# Revit family: BE_84401_de_DE
name_source: partatom
category: Leuchten
revit_build: Autodesk Revit 2015 (Build: 20160512_0715(x64)
units: mm (PartAtom-declared; Revit-internal decimal feet)

## types (4) — shared parameters
AC/DC = AC/DC
Aktualisierung = 2017-07-06T04:09:10
Anschlussleitung = 6.0 m X05BQ-F 4 × 1²
BEGA_Dummy = Nein
BEGA_IES = Ja
BEGA_IES1 = Ja
BEGA_IES2 = Ja
BEGA_IES3 = Ja
BEGA_Intern = Ja
BEGA_Intern_Konstruktion = Ja
BEGA_Intern_an = Ja
BEGA_Intern_aus = Ja
Beschreibung = Aufsatzleuchte
Beschreibung_Sonderanfertigung = Hier können Sie Informationen zur Sonderanfertigung eintragen.
CE_Konformität = ja
Einstecktiefe = 60 mm
Energieeffizienzklasse = LED A++ - A
Farbfilter = 16777215
Farbtemperaturverschiebung bei Dämpfen der Lampe = <Keine Auswahl>
Farbwiedergabeindex = Ra > 80
Frequenz = 0/50-60 Hz
Gewicht = 14.6 kg
Hersteller = BEGA
Lampe = LED 23.4 W
Lastklassifizierung = Beleuchtung
Lebensdauerkriterien = L70B50 @ 25 °C = 310000 h
Logo = BEGA_Logo.png
M_W = Nein
Material_02 = BEGA_Oberfläche_Silber_matt
Material_03 = BEGA_Oberfläche_Weiss_matt
Material_06 = BEGA_Oberfläche_Edelstahl_gebürstet
Material_09 = BEGA_Glas_klar
Material_10 = BEGA_Glas_matt
Material_11 = BEGA_Glas_opal
Material_15 = BEGA_Leuchtmedium_matt
Material_17 = BEGA_Reflektor
Material_18 = BEGA_Gummi_schwarz
Neigungswinkel = 0.00°
Produktdatenblatt = http://www.bega.de
Scheinlast = 0 VA
Schutzart = IP 65
Schutzklasse = II
Sonderanfertigung = Nein
Spannung = 240 V
Typenbild = 84401.png
URL = http://www.bega.de
Umgebungstemperatur = 25 °C
Windangriffsfläche = 0.14 m²
zero-valued in all types: BEGA_IES_X1, BEGA_IES_X2, BEGA_IES_Y1, BEGA_IES_Y2, BEGA_IES_Z1, BEGA_IES_Z2, Vorgabe-Ansicht

## per-type parameters (varying)
| type | Bestellnummer | Datei für fotometrisches Netz | Farbtemperatur | LED_Modulbezeichnung | Lampenlichtstrom | Leuchtenlichtstrom | M_A | M_G | Modell |
| BEGA_84401_Grafit_K3 | 84401K3 | BE_84401K3.IES | 3000 K | 6x LED-0146/830 | 4350 lm | 2170 lm | Nein | Ja | 84401K3 |
| BEGA_84401_Grafit_K4 | 84401 | BE_84401.IES | 4000 K | 6x LED-0146/840 | 4470 lm | 2230 lm | Nein | Ja | 84401 |
| BEGA_84401_Silber_K3 | 84401AK3 | BE_84401K3.IES | 3000 K | 6x LED-0146/830 | 4350 lm | 2170 lm | Ja | Nein | 84401AK3 |
| BEGA_84401_Silber_K4 | 84401A | BE_84401.IES | 4000 K | 6x LED-0146/840 | 4470 lm | 2230 lm | Ja | Nein | 84401A |
